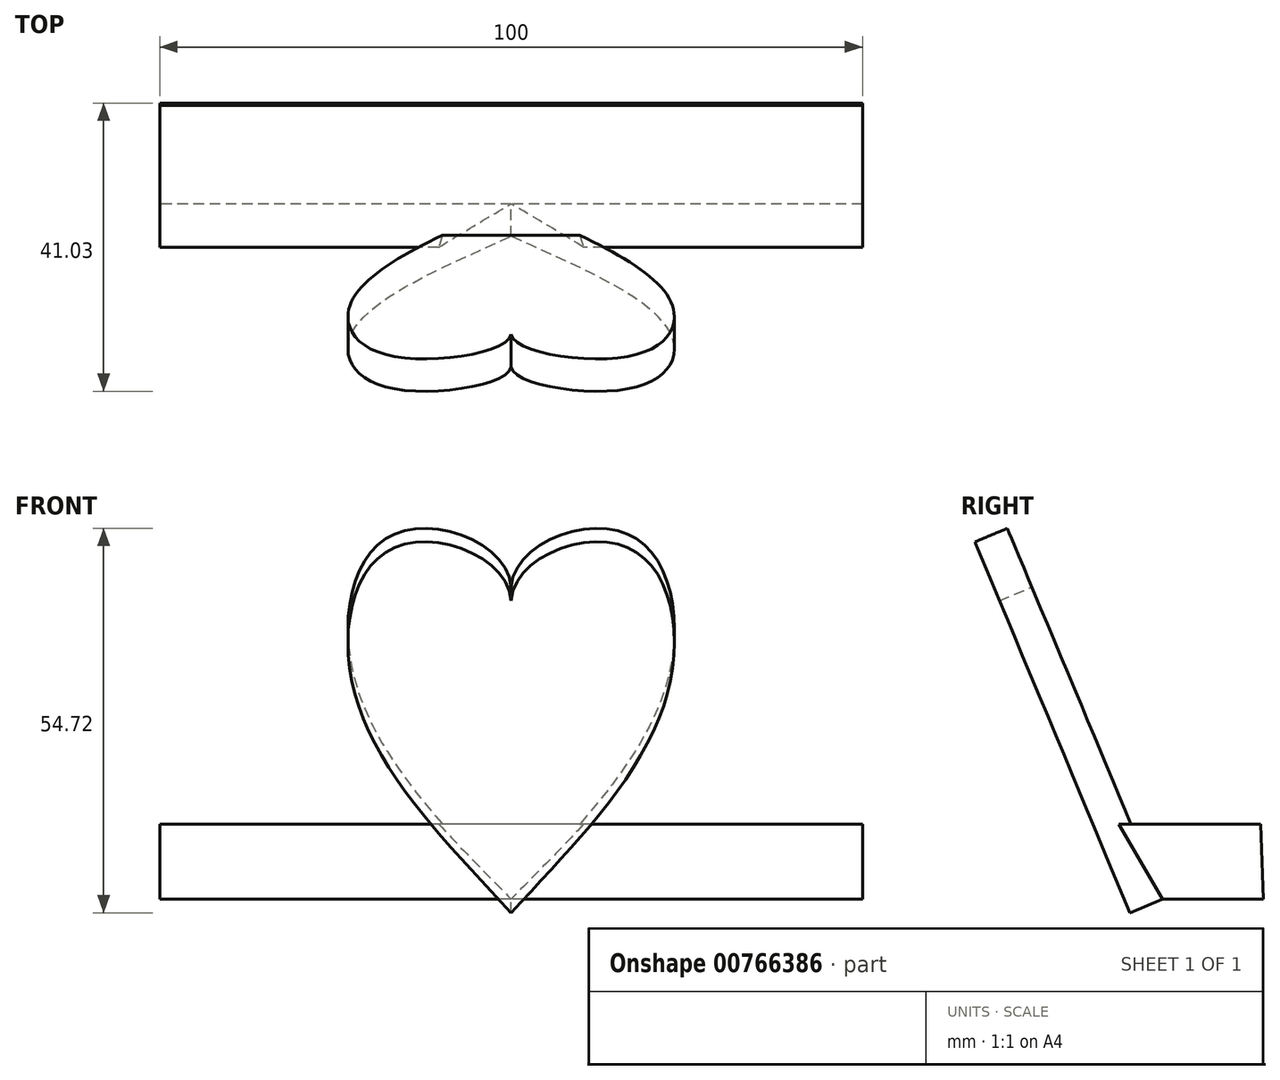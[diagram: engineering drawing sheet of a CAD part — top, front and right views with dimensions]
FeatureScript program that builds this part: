
annotation { "Feature Type Name" : "Feature", "Feature Type Description" : "" }
export const myFeature = defineFeature(function(context is Context, id is Id, definition is map)
    precondition{}
    {
        {
            var Q0;
            Q0=qCreatedBy(makeId("Right.planeOp"),FACE);
            var sketch = newSketch(context, id + "F0", { "sketchPlane" : qUnion([Q0])});
            skLineSegment(sketch, "E0", {"start": v(-17.4, 41.64) * mm, "end": v(0, 0) * mm});
            skLineSegment(sketch, "E1", {"start": v(0, 0) * mm, "end": v(50.65, 0) * mm});
            skSolve(sketch);
        }
        {
            var Q0;
            Q0=sQuery(id+"F0.wireOp",EDGE,"E0");
            cPlane(context, id + "F1", {"entities" : qUnion([Q0]), "cplaneType" : CPlaneType.LINE_ANGLE, "offset" : 25 * mm, "angle" : 90 * degree, "oppositeDirection" : true, "width" : 150 * mm, "height" : 150 * mm});
        }
        {
            var Q0;
            Q0=qCreatedBy(id+"F1.planeOp",FACE);
            var sketch = newSketch(context, id + "F2", { "sketchPlane" : qUnion([Q0])});
            skFitSpline(sketch, "E2", {"points": [v(0, 48.15) * mm, v(15.84, 56.64) * mm, v(22.34, 34.2) * mm, v(0, 0) * mm], "startDerivative": vector(4.6, 71.87) * mm, "endDerivative": vector(-64.57, -76.4) * mm});
            skFitSpline(sketch, "E3.MirrorCS", {"points": [v(0, 48.15) * mm, v(-15.84, 56.64) * mm, v(-22.34, 34.2) * mm, v(0, 0) * mm], "startDerivative": vector(-4.6, 71.87) * mm, "endDerivative": vector(64.57, -76.4) * mm});
            skSolve(sketch);
        }
        {
            var Q0;
            Q0=makeQuery(id+"F2.imprint","IMPRINT",FACE,{"disambiguationData":[TD([[makeQuery(id+"F2.imprint","IMPRINT",EDGE,{"derivedFrom":sQuery(id+"F2.wireOp",EDGE,"E2")}),-1.0]])]});
            extrude(context, id + "F3", {"entities" : qUnion([Q0]), "depth" : 5 * mm, "offsetDistance" : 25 * mm});
        }
        {
            var Q0;
            Q0=qCreatedBy(makeId("Right.planeOp"),FACE);
            var sketch = newSketch(context, id + "F4", { "sketchPlane" : qUnion([Q0])});
            skLineSegment(sketch, "E4", {"start": v(0, 0) * mm, "end": v(14.35, 0) * mm});
            skLineSegment(sketch, "E5", {"start": v(0, 0) * mm, "end": v(-6.18, 10.7) * mm});
            skLineSegment(sketch, "E6", {"start": v(-6.18, 10.7) * mm, "end": v(14.01, 10.7) * mm});
            skLineSegment(sketch, "E7", {"start": v(14.01, 10.7) * mm, "end": v(14.35, 0) * mm});
            skSolve(sketch);
        }
        {
            var Q0;
            Q0=makeQuery(id+"F4.imprint","IMPRINT",FACE,{"disambiguationData":[TD([[makeQuery(id+"F4.imprint","IMPRINT",EDGE,{"derivedFrom":sQuery(id+"F4.wireOp",EDGE,"E4")}),1.0]])]});
            extrude(context, id + "F5", {"entities" : qUnion([Q0]), "operationType" : NewBodyOperationType.ADD, "endBound" : BoundingType.SYMMETRIC, "depth" : 100 * mm, "offsetDistance" : 25 * mm});
        }
    });
